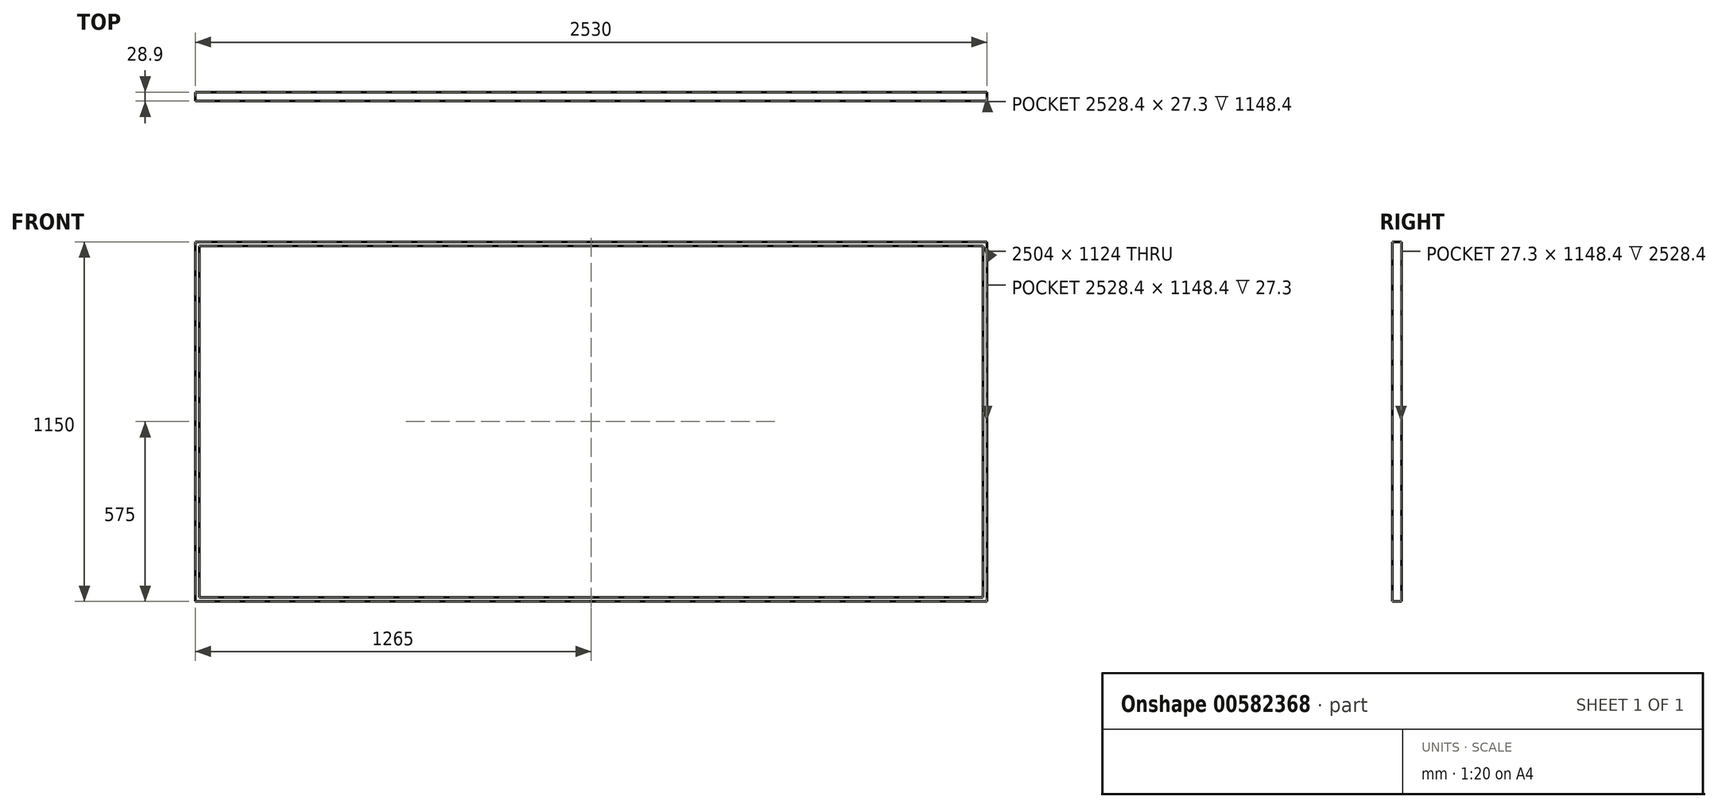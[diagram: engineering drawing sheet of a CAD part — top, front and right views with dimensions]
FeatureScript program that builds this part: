
annotation { "Feature Type Name" : "Feature", "Feature Type Description" : "" }
export const myFeature = defineFeature(function(context is Context, id is Id, definition is map)
    precondition{}
    {
        {
            var Q0;
            Q0=qCreatedBy(makeId("Front.planeOp"),FACE);
            var sketch = newSketch(context, id + "F0", { "sketchPlane" : qUnion([Q0])});
            skLineSegment(sketch, "E0.bottom", {"start": v(0, 0) * mm, "end": v(2530, 0) * mm});
            skLineSegment(sketch, "E0.top", {"start": v(0, 1150) * mm, "end": v(2530, 1150) * mm});
            skLineSegment(sketch, "E0.left", {"start": v(0, 0) * mm, "end": v(0, 1150) * mm});
            skLineSegment(sketch, "E0.right", {"start": v(2530, 0) * mm, "end": v(2530, 1150) * mm});
            skSolve(sketch);
        }
        {
            var Q0;
            Q0=makeQuery(id+"F0.imprint","IMPRINT",FACE,{"disambiguationData":[TD([[makeQuery(id+"F0.imprint","IMPRINT",EDGE,{"derivedFrom":sQuery(id+"F0.wireOp",EDGE,"E0.bottom")}),1.0]])]});
            extrude(context, id + "F1", {"entities" : qUnion([Q0]), "depth" : 28.9 * mm, "offsetDistance" : 25 * mm});
        }
        {
            var Q0;
            Q0=makeQuery(id+"F1.opExtrude","CAP_FACE",FACE,{"disambiguationData":[OSD([sQuery(id+"F0.wireOp",EDGE,"E0.bottom"),sQuery(id+"F0.wireOp",EDGE,"E0.top"),sQuery(id+"F0.wireOp",EDGE,"E0.left"),sQuery(id+"F0.wireOp",EDGE,"E0.right")])],"isStart":false});
            var sketch = newSketch(context, id + "F2", { "sketchPlane" : qUnion([Q0])});
            skLineSegment(sketch, "E1.bottom", {"start": v(2517, 1137) * mm, "end": v(13, 1137) * mm});
            skLineSegment(sketch, "E1.top", {"start": v(2517, 13) * mm, "end": v(13, 13) * mm});
            skLineSegment(sketch, "E1.left", {"start": v(2517, 1137) * mm, "end": v(2517, 13) * mm});
            skLineSegment(sketch, "E1.right", {"start": v(13, 1137) * mm, "end": v(13, 13) * mm});
            skSolve(sketch);
        }
        {
            var Q0;
            Q0=makeQuery(id+"F2.imprint","IMPRINT",FACE,{"disambiguationData":[TD([[makeQuery(id+"F2.imprint","IMPRINT",EDGE,{"derivedFrom":sQuery(id+"F2.wireOp",EDGE,"E1.bottom")}),1.0]])]});
            extrude(context, id + "F3", {"entities" : qUnion([Q0]), "operationType" : NewBodyOperationType.REMOVE, "oppositeDirection" : true, "depth" : 28.1 * mm, "offsetDistance" : 25 * mm});
        }
        {
            var Q0;
            Q0=makeQuery(id+"F3.boolean.opBoolean","COPY",FACE,{"derivedFrom":makeQuery(id+"F3.opExtrude","CAP_FACE",FACE,{"disambiguationData":[OSD([sQuery(id+"F2.wireOp",EDGE,"E1.bottom"),sQuery(id+"F2.wireOp",EDGE,"E1.top"),sQuery(id+"F2.wireOp",EDGE,"E1.left"),sQuery(id+"F2.wireOp",EDGE,"E1.right")])],"isStart":false})});
            var sketch = newSketch(context, id + "F4", { "sketchPlane" : qUnion([Q0])});
            skLineSegment(sketch, "E2.bottom", {"start": v(0.8, 1149.2) * mm, "end": v(2529.2, 1149.2) * mm});
            skLineSegment(sketch, "E2.top", {"start": v(0.8, 0.8) * mm, "end": v(2529.2, 0.8) * mm});
            skLineSegment(sketch, "E2.left", {"start": v(0.8, 1149.2) * mm, "end": v(0.8, 0.8) * mm});
            skLineSegment(sketch, "E2.right", {"start": v(2529.2, 1149.2) * mm, "end": v(2529.2, 0.8) * mm});
            skSolve(sketch);
        }
        {
            var Q0;
            Q0 = qSketchRegion(id + "F4", true);
            extrude(context, id + "F5", {"entities" : qUnion([Q0]), "operationType" : NewBodyOperationType.REMOVE, "depth" : 27.3 * mm, "offsetDistance" : 25 * mm});
        }
    });
